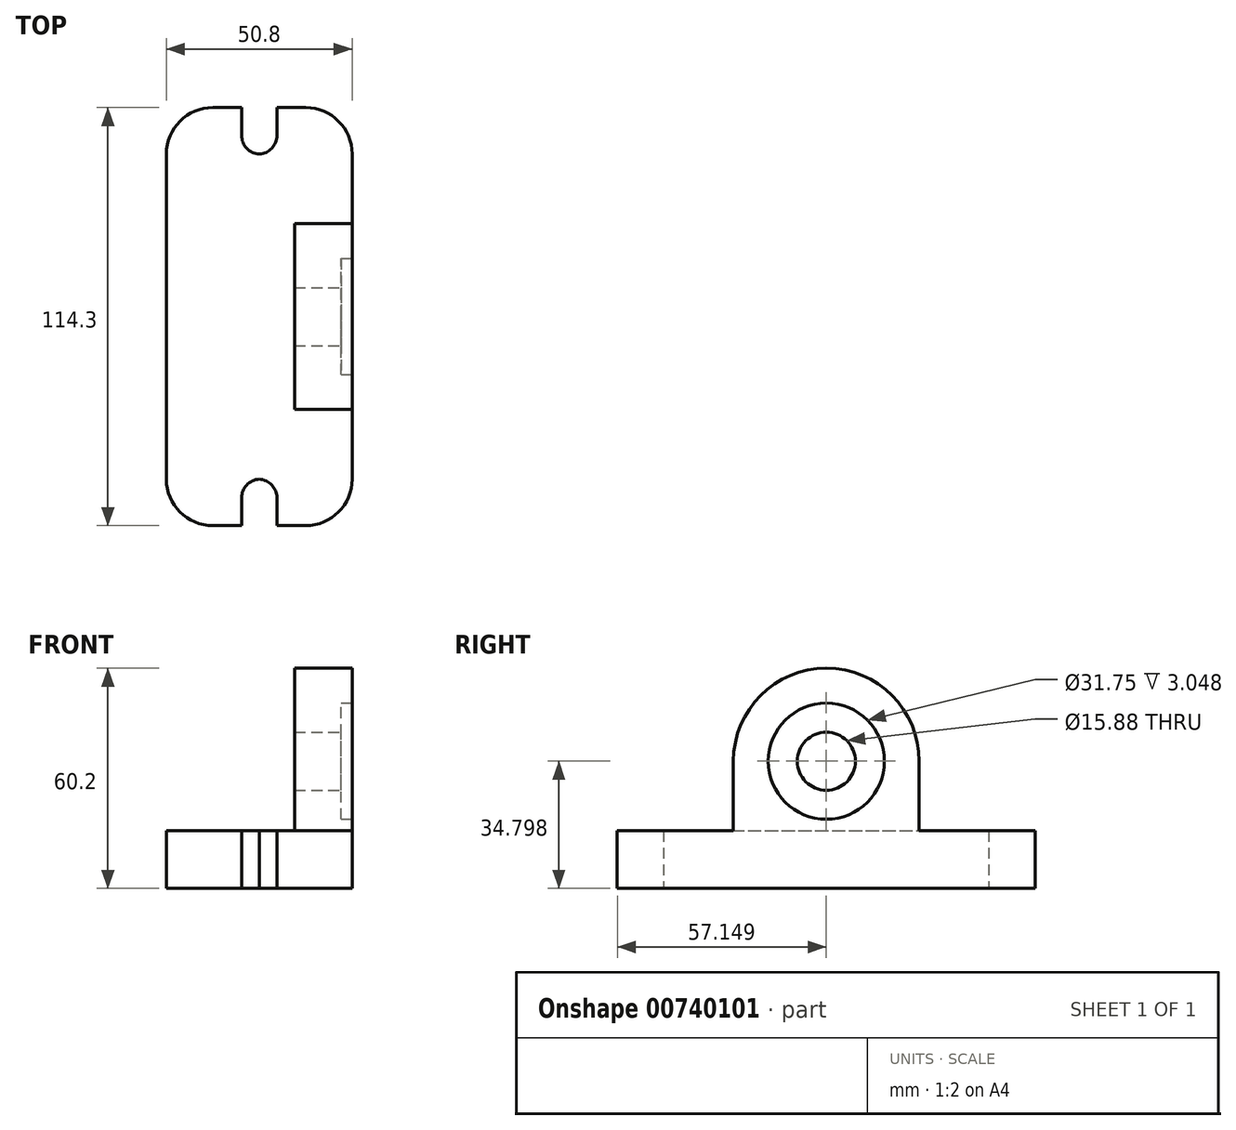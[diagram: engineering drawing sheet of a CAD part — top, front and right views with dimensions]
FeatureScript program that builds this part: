
annotation { "Feature Type Name" : "Feature", "Feature Type Description" : "" }
export const myFeature = defineFeature(function(context is Context, id is Id, definition is map)
    precondition{}
    {
        {
            var Q0;
            Q0=qCreatedBy(makeId("Top.planeOp"),FACE);
            var sketch = newSketch(context, id + "F0", { "sketchPlane" : qUnion([Q0])});
            skLineSegment(sketch, "E0.bottom", {"start": v(-27.77, -47.76) * mm, "end": v(23.03, -47.76) * mm});
            skLineSegment(sketch, "E0.top", {"start": v(-27.77, 66.54) * mm, "end": v(23.03, 66.54) * mm});
            skLineSegment(sketch, "E0.left", {"start": v(-27.77, -47.76) * mm, "end": v(-27.77, 66.54) * mm});
            skLineSegment(sketch, "E0.right", {"start": v(23.03, -47.76) * mm, "end": v(23.03, 66.54) * mm});
            skSolve(sketch);
        }
        {
            var Q0;
            Q0 = qSketchRegion(id + "F0", true);
            extrude(context, id + "F1", {"entities" : qUnion([Q0]), "depth" : 15.75 * mm, "offsetDistance" : 25.4 * mm});
        }
        {
            var Q0;
            Q0=makeQuery(id+"F1.opExtrude","CAP_FACE",FACE,{"disambiguationData":[OSD([sQuery(id+"F0.wireOp",EDGE,"E0.bottom"),sQuery(id+"F0.wireOp",EDGE,"E0.top"),sQuery(id+"F0.wireOp",EDGE,"E0.left"),sQuery(id+"F0.wireOp",EDGE,"E0.right")])],"isStart":false});
            var sketch = newSketch(context, id + "F2", { "sketchPlane" : qUnion([Q0])});
            skLineSegment(sketch, "E1.bottom", {"start": v(-7.2, 53.84) * mm, "end": v(2.46, 53.84) * mm});
            skLineSegment(sketch, "E1.top", {"start": v(-7.2, 79.24) * mm, "end": v(2.46, 79.24) * mm});
            skLineSegment(sketch, "E1.left", {"start": v(-7.2, 53.84) * mm, "end": v(-7.2, 79.24) * mm});
            skLineSegment(sketch, "E1.right", {"start": v(2.46, 53.84) * mm, "end": v(2.46, 79.24) * mm});
            skPoint(sketch, "E1.middle", {"position": v(-2.37, 66.54) * mm});
            skLineSegment(sketch, "E2.bottom", {"start": v(-7.2, -35.06) * mm, "end": v(2.46, -35.06) * mm});
            skLineSegment(sketch, "E2.top", {"start": v(-7.2, -60.46) * mm, "end": v(2.46, -60.46) * mm});
            skLineSegment(sketch, "E2.left", {"start": v(-7.2, -35.06) * mm, "end": v(-7.2, -60.46) * mm});
            skLineSegment(sketch, "E2.right", {"start": v(2.46, -35.06) * mm, "end": v(2.46, -60.46) * mm});
            skPoint(sketch, "E2.middle", {"position": v(-2.37, -47.76) * mm});
            skSolve(sketch);
        }
        {
            var Q0;
            {var subQ0=sQuery(id+"F2.wireOp",EDGE,"E2.bottom");Q0=makeQuery(id+"F2.imprint","IMPRINT",FACE,{"disambiguationData":[TD([[makeQuery(id+"F2.imprint","IMPRINT",EDGE,{"derivedFrom":subQ0}),-1.0]])]});}
            var Q1;
            {var subQ0=sQuery(id+"F2.wireOp",EDGE,"E1.bottom");Q1=makeQuery(id+"F2.imprint","IMPRINT",FACE,{"disambiguationData":[TD([[makeQuery(id+"F2.imprint","IMPRINT",EDGE,{"derivedFrom":subQ0}),1.0]])]});}
            extrude(context, id + "F3", {"entities" : qUnion([Q0, Q1]), "operationType" : NewBodyOperationType.REMOVE, "oppositeDirection" : true, "depth" : 25.4 * mm, "offsetDistance" : 25.4 * mm});
        }
        {
            var Q0;
            Q0=makeQuery(id+"F1.opExtrude","SWEPT_EDGE",EDGE,{"disambiguationData":[OSD([sQuery(id+"F0.wireOp",EDGE,"E0.top"),sQuery(id+"F0.wireOp",EDGE,"E0.left")])]});
            var Q1;
            Q1=makeQuery(id+"F1.opExtrude","SWEPT_EDGE",EDGE,{"disambiguationData":[OSD([sQuery(id+"F0.wireOp",EDGE,"E0.top"),sQuery(id+"F0.wireOp",EDGE,"E0.right")])]});
            var Q2;
            Q2=makeQuery(id+"F1.opExtrude","SWEPT_EDGE",EDGE,{"disambiguationData":[OSD([sQuery(id+"F0.wireOp",EDGE,"E0.bottom"),sQuery(id+"F0.wireOp",EDGE,"E0.left")])]});
            var Q3;
            Q3=makeQuery(id+"F1.opExtrude","SWEPT_EDGE",EDGE,{"disambiguationData":[OSD([sQuery(id+"F0.wireOp",EDGE,"E0.bottom"),sQuery(id+"F0.wireOp",EDGE,"E0.right")])]});
            fillet(context, id + "F4", {"entities" : qUnion([Q0, Q1, Q2, Q3]), "radius" : 12.7 * mm, "tangentPropagation" : true, "allowEdgeOverflow" : false});
        }
        {
            var Q0;
            Q0=makeQuery(id+"F3.boolean.opBoolean","COPY",EDGE,{"derivedFrom":makeQuery(id+"F3.opExtrude","SWEPT_EDGE",EDGE,{"disambiguationData":[OSD([sQuery(id+"F2.wireOp",EDGE,"E1.bottom"),sQuery(id+"F2.wireOp",EDGE,"E1.right")])]})});
            var Q1;
            Q1=makeQuery(id+"F3.boolean.opBoolean","COPY",EDGE,{"derivedFrom":makeQuery(id+"F3.opExtrude","SWEPT_EDGE",EDGE,{"disambiguationData":[OSD([sQuery(id+"F2.wireOp",EDGE,"E1.bottom"),sQuery(id+"F2.wireOp",EDGE,"E1.left")])]})});
            var Q2;
            Q2=makeQuery(id+"F3.boolean.opBoolean","COPY",EDGE,{"derivedFrom":makeQuery(id+"F3.opExtrude","SWEPT_EDGE",EDGE,{"disambiguationData":[OSD([sQuery(id+"F2.wireOp",EDGE,"E2.bottom"),sQuery(id+"F2.wireOp",EDGE,"E2.right")])]})});
            var Q3;
            Q3=makeQuery(id+"F3.boolean.opBoolean","COPY",EDGE,{"derivedFrom":makeQuery(id+"F3.opExtrude","SWEPT_EDGE",EDGE,{"disambiguationData":[OSD([sQuery(id+"F2.wireOp",EDGE,"E2.bottom"),sQuery(id+"F2.wireOp",EDGE,"E2.left")])]})});
            fillet(context, id + "F5", {"entities" : qUnion([Q0, Q1, Q2, Q3]), "radius" : 5.08 * mm, "tangentPropagation" : true, "allowEdgeOverflow" : false});
        }
        {
            var Q0;
            Q0=makeQuery(id+"F1.opExtrude","SWEPT_FACE",FACE,{"disambiguationData":[OSD([sQuery(id+"F0.wireOp",EDGE,"E0.right")])]});
            var sketch = newSketch(context, id + "F6", { "sketchPlane" : qUnion([Q0])});
            skArc(sketch, "E3", {"start": v(34.79, 34.8) * mm, "mid": v(9.39, 60.2) * mm, "end": v(-16.01, 34.8) * mm});
            skLineSegment(sketch, "E4", {"start": v(-16.01, 34.8) * mm, "end": v(-16.01, 15.75) * mm});
            skLineSegment(sketch, "E5", {"start": v(34.79, 34.8) * mm, "end": v(34.79, 15.75) * mm});
            skPoint(sketch, "E6.start.orphan", {"position": v(9.39, 15.75) * mm});
            skSolve(sketch);
        }
        {
            var Q0;
            Q0=makeQuery(id+"F6.imprint","IMPRINT",FACE,{"disambiguationData":[TD([[makeQuery(id+"F6.imprint","IMPRINT",EDGE,{"derivedFrom":sQuery(id+"F6.wireOp",EDGE,"E3")}),1.0]])]});
            extrude(context, id + "F7", {"entities" : qUnion([Q0]), "operationType" : NewBodyOperationType.ADD, "oppositeDirection" : true, "depth" : 15.75 * mm, "offsetDistance" : 25.4 * mm});
        }
        {
            var Q0;
            {var subQ0=sQuery(id+"F0.wireOp",EDGE,"E0.right");Q0=makeQuery(id+"F7.boolean.opBoolean","MERGE",FACE,{"derivedFrom":[makeQuery(id+"F1.opExtrude","SWEPT_FACE",FACE,{"disambiguationData":[OSD([subQ0])]}),makeQuery(id+"F7.opExtrude","CAP_FACE",FACE,{"disambiguationData":[OSD([subQ0,sQuery(id+"F6.wireOp",EDGE,"E3"),sQuery(id+"F6.wireOp",EDGE,"E4"),sQuery(id+"F6.wireOp",EDGE,"E5")])],"isStart":true})]});}
            var sketch = newSketch(context, id + "F8", { "sketchPlane" : qUnion([Q0])});
            skCircle(sketch, "E7", {"center": v(9.39, 34.8) * mm, "radius": 15.88 * mm});
            skSolve(sketch);
        }
        {
            var Q0;
            Q0=makeQuery(id+"F8.imprint","IMPRINT",FACE,{"disambiguationData":[TD([[makeQuery(id+"F8.imprint","IMPRINT",EDGE,{"derivedFrom":sQuery(id+"F8.wireOp",EDGE,"E7")}),1.0]])]});
            extrude(context, id + "F9", {"entities" : qUnion([Q0]), "operationType" : NewBodyOperationType.REMOVE, "oppositeDirection" : true, "depth" : 3.05 * mm, "offsetDistance" : 25.4 * mm});
        }
        {
            var Q0;
            Q0=makeQuery(id+"F9.boolean.opBoolean","COPY",FACE,{"derivedFrom":makeQuery(id+"F9.opExtrude","CAP_FACE",FACE,{"disambiguationData":[OSD([sQuery(id+"F8.wireOp",EDGE,"E7")])],"isStart":false})});
            var sketch = newSketch(context, id + "F10", { "sketchPlane" : qUnion([Q0])});
            skCircle(sketch, "E8", {"center": v(9.39, 34.8) * mm, "radius": 7.94 * mm});
            skSolve(sketch);
        }
        {
            var Q0;
            Q0=makeQuery(id+"F10.imprint","IMPRINT",FACE,{"disambiguationData":[TD([[makeQuery(id+"F10.imprint","IMPRINT",EDGE,{"derivedFrom":sQuery(id+"F10.wireOp",EDGE,"E8")}),1.0]])]});
            extrude(context, id + "F11", {"entities" : qUnion([Q0]), "operationType" : NewBodyOperationType.REMOVE, "oppositeDirection" : true, "depth" : 25.4 * mm, "offsetDistance" : 25.4 * mm});
        }
    });
